# Revit family: Access_Door-Heavy_Duty-Best Access Doors-Large_Openings-Drywall_Flange-(BA-LO1D-DF)
name_source: partatom
category: Specialty Equipment
revit_build: Autodesk Revit 2017 (Build: 20160225_1515(x64)
units: mm (PartAtom-declared; Revit-internal decimal feet)

## family parameters
Cut with Voids When Loaded = No
Host = Face
OmniClass Number = 23.30.10.27.17
Part Type = Normal
Room Calculation Point = No
Round Connector Dimension = Use Diameter
Shared = No

## types (2) — shared parameters
Assembly Code = C1020700
Construction Material = Metal - Best Access Doors - Aluminum
Default Elevation = 0"
Description = Heavy duty access door for large openings
Door Height = 48"
Door Height Calc = 48"
Door Width = 48"
Door Width Calc = 48"
Finish = Metal - Best Access Doors - Powder Coated White
Frame Depth = 2"
Height Actual = 50"
Manufacturer = Best Access Doors
Model = BA-LO1D-DF
Product data url = https://bimobject.com
Width Actual = 50"

## per-type parameters (varying)
| type | URL |
| 48 x 48 | https://www.bestaccessdoors.com |
| Custom | http://www.bestaccessdoors.com |

## geometry (parser evidence)
native form markers: Blend x4, Sweep x20
no freeform markers — native parametric forms only
